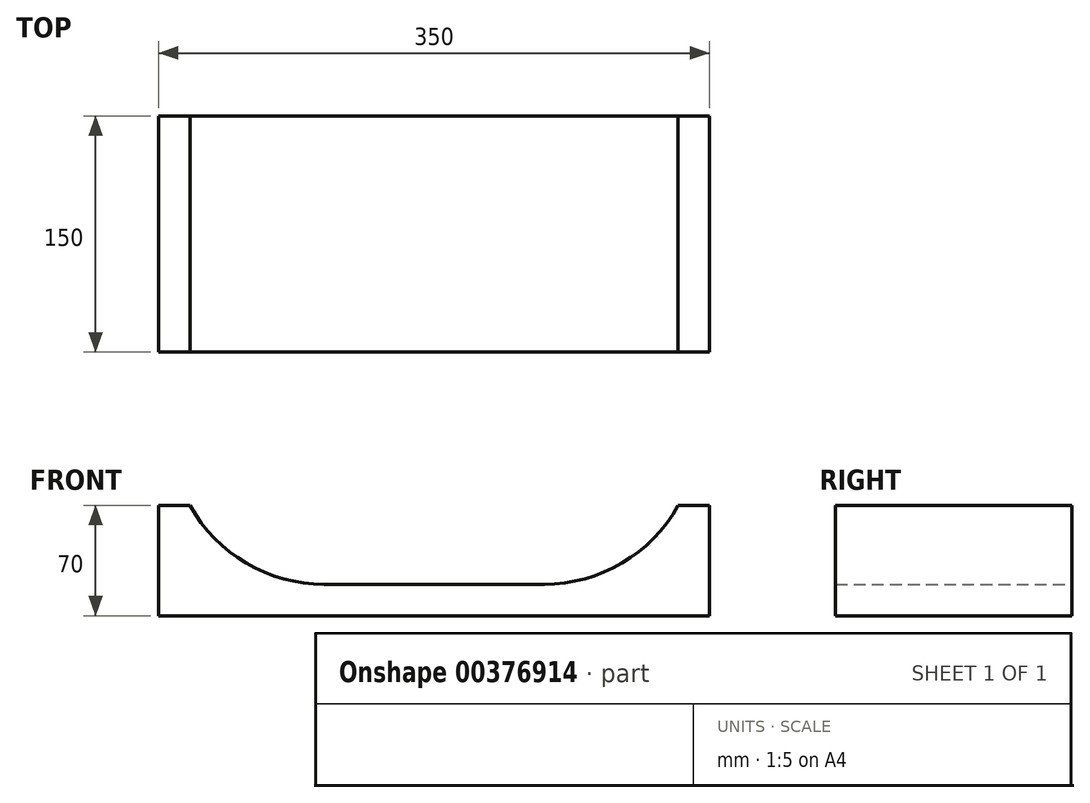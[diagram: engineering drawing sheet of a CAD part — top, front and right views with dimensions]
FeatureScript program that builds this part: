
annotation { "Feature Type Name" : "Feature", "Feature Type Description" : "" }
export const myFeature = defineFeature(function(context is Context, id is Id, definition is map)
    precondition{}
    {
        {
            var Q0;
            Q0=qCreatedBy(makeId("Front.planeOp"),FACE);
            var sketch = newSketch(context, id + "F0", { "sketchPlane" : qUnion([Q0])});
            skLineSegment(sketch, "E0", {"start": v(-63.12, 78.1) * mm, "end": v(-63.12, 8.1) * mm});
            skLineSegment(sketch, "E1", {"start": v(-63.12, 8.1) * mm, "end": v(286.88, 8.1) * mm});
            skLineSegment(sketch, "E2", {"start": v(286.88, 8.1) * mm, "end": v(286.88, 78.1) * mm});
            skLineSegment(sketch, "E3", {"start": v(-63.12, 78.1) * mm, "end": v(-43.12, 78.1) * mm});
            skLineSegment(sketch, "E4", {"start": v(286.88, 78.1) * mm, "end": v(266.88, 78.1) * mm});
            skLineSegment(sketch, "E5", {"start": v(111.88, 28.1) * mm, "end": v(181.88, 28.1) * mm});
            skLineSegment(sketch, "E6", {"start": v(181.88, 28.1) * mm, "end": v(41.88, 28.1) * mm});
            skPoint(sketch, "E6.endSnap0", {"position": v(146.88, 28.1) * mm});
            skArc(sketch, "E7", {"start": v(41.88, 28.1) * mm, "mid": v(-7.43, 41.52) * mm, "end": v(-43.12, 78.1) * mm});
            skArc(sketch, "E8", {"start": v(181.88, 28.1) * mm, "mid": v(231.19, 41.52) * mm, "end": v(266.88, 78.1) * mm});
            skSolve(sketch);
        }
        {
            var Q0;
            Q0=makeQuery(id+"F0.imprint","IMPRINT",FACE,{"disambiguationData":[TD([[makeQuery(id+"F0.imprint","IMPRINT",EDGE,{"derivedFrom":sQuery(id+"F0.wireOp",EDGE,"E0")}),1.0]])]});
            extrude(context, id + "F1", {"entities" : qUnion([Q0]), "depth" : 150 * mm});
        }
    });
